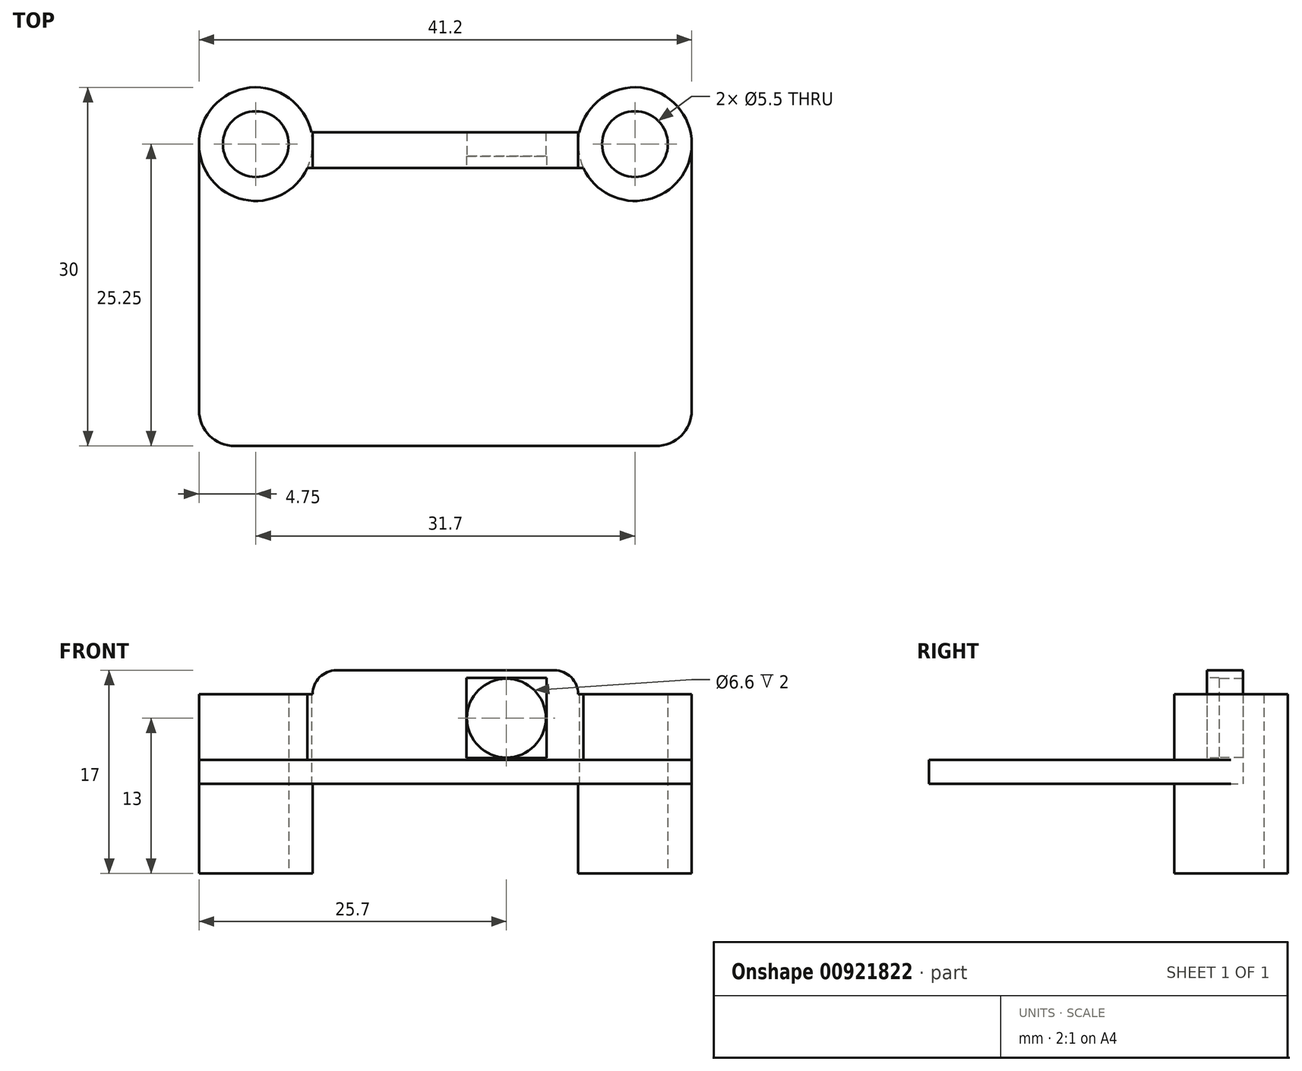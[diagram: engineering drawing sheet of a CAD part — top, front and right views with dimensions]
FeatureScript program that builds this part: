
annotation { "Feature Type Name" : "Feature", "Feature Type Description" : "" }
export const myFeature = defineFeature(function(context is Context, id is Id, definition is map)
    precondition{}
    {
        {
            var Q0;
            Q0=qCreatedBy(makeId("Top.planeOp"),FACE);
            var sketch = newSketch(context, id + "F0", { "sketchPlane" : qUnion([Q0])});
            skLineSegment(sketch, "E0.bottom", {"start": v(15.85, 15) * mm, "end": v(-15.85, 15) * mm});
            skLineSegment(sketch, "E0.top", {"start": v(17.6, -15) * mm, "end": v(-17.6, -15) * mm});
            skLineSegment(sketch, "E0.left", {"start": v(20.6, 10.25) * mm, "end": v(20.6, -12) * mm});
            skLineSegment(sketch, "E0.right", {"start": v(-20.6, 10.25) * mm, "end": v(-20.6, -12) * mm});
            skPoint(sketch, "E0.middle", {"position": v(0, 0) * mm});
            skCircle(sketch, "E1", {"center": v(-15.85, 10.25) * mm, "radius": 2.75 * mm});
            skLineSegment(sketch, "E2", {"start": v(-15.85, 10.25) * mm, "end": v(15.85, 10.25) * mm, "construction": true});
            skCircle(sketch, "E3", {"center": v(15.85, 10.25) * mm, "radius": 2.75 * mm});
            skPoint(sketch, "E4.visualSharp", {"position": v(-20.6, 15) * mm});
            skPoint(sketch, "E5.visualSharp", {"position": v(20.6, 15) * mm});
            skPoint(sketch, "E6.visualSharp", {"position": v(20.6, -15) * mm});
            skArc(sketch, "E6.filletArc", {"start": v(17.6, -15) * mm, "mid": v(19.72, -14.12) * mm, "end": v(20.6, -12) * mm});
            skPoint(sketch, "E7.visualSharp", {"position": v(-20.6, -15) * mm});
            skArc(sketch, "E7.filletArc", {"start": v(-20.6, -12) * mm, "mid": v(-19.72, -14.12) * mm, "end": v(-17.6, -15) * mm});
            skCircle(sketch, "E8.0", {"center": v(-15.85, 10.25) * mm, "radius": 4.75 * mm});
            skCircle(sketch, "E9.0", {"center": v(15.85, 10.25) * mm, "radius": 4.75 * mm});
            skSolve(sketch);
        }
        {
            var Q0;
            {var subQ2=sQuery(id+"F0.wireOp",EDGE,"E0.bottom");Q0=makeQuery(id+"F0.imprint","IMPRINT",FACE,{"disambiguationData":[TD([[makeQuery(id+"F0.imprint","IMPRINT",EDGE,{"derivedFrom":subQ2}),1.0]])]});}
            extrude(context, id + "F1", {"entities" : qUnion([Q0]), "depth" : 2 * mm, "offsetDistance" : 25 * mm});
        }
        {
            var Q0;
            Q0=makeQuery(id+"F0.imprint","IMPRINT",FACE,{"disambiguationData":[TD([[makeQuery(id+"F0.imprint","IMPRINT",EDGE,{"derivedFrom":sQuery(id+"F0.wireOp",EDGE,"E1")}),-1.0]])]});
            var Q1;
            Q1=makeQuery(id+"F0.imprint","IMPRINT",FACE,{"disambiguationData":[TD([[makeQuery(id+"F0.imprint","IMPRINT",EDGE,{"derivedFrom":sQuery(id+"F0.wireOp",EDGE,"E3")}),-1.0]])]});
            extrude(context, id + "F2", {"entities" : qUnion([Q0, Q1]), "operationType" : NewBodyOperationType.ADD, "endBound" : BoundingType.SYMMETRIC, "depth" : 15 * mm, "offsetDistance" : 25 * mm});
        }
        {
            var Q0;
            Q0=sQuery(id+"F0.wireOp",EDGE,"E2");
            cPlane(context, id + "F3", {"entities" : qUnion([Q0]), "cplaneType" : CPlaneType.LINE_ANGLE, "offset" : 25 * mm, "angle" : 0 * degree, "width" : 150 * mm, "height" : 150 * mm});
        }
        {
            var Q0;
            Q0=qCreatedBy(id+"F3.planeOp",FACE);
            var sketch = newSketch(context, id + "F4", { "sketchPlane" : qUnion([Q0])});
            skLineSegment(sketch, "E10", {"start": v(-11.1, 7.5) * mm, "end": v(-11.1, 7.5) * mm});
            skLineSegment(sketch, "E11", {"start": v(11.1, -7.5) * mm, "end": v(11.1, 2) * mm});
            skLineSegment(sketch, "E12.0", {"start": v(-15.85, 2) * mm, "end": v(15.85, 2) * mm});
            skLineSegment(sketch, "E13", {"start": v(-9.1, 9.5) * mm, "end": v(9.1, 9.5) * mm});
            skPoint(sketch, "E14.visualSharp", {"position": v(-11.1, 9.5) * mm});
            skArc(sketch, "E14.filletArc", {"start": v(-9.1, 9.5) * mm, "mid": v(-10.51, 8.91) * mm, "end": v(-11.1, 7.5) * mm});
            skPoint(sketch, "E15.visualSharp", {"position": v(11.1, 9.5) * mm});
            skArc(sketch, "E15.filletArc", {"start": v(11.1, 7.5) * mm, "mid": v(10.51, 8.91) * mm, "end": v(9.1, 9.5) * mm});
            skCircle(sketch, "E16", {"center": v(-5.1, 5.5) * mm, "radius": 3.3 * mm});
            skLineSegment(sketch, "E17.0", {"start": v(-20.6, 7.5) * mm, "end": v(-11.1, 7.5) * mm});
            skLineSegment(sketch, "E18", {"start": v(-13.1, 7.5) * mm, "end": v(-13.1, 2) * mm});
            skLineSegment(sketch, "E19.MirrorCS", {"start": v(13.1, 7.5) * mm, "end": v(13.1, 2) * mm});
            skLineSegment(sketch, "E20.trimOffspring", {"start": v(-11.1, 2) * mm, "end": v(-11.1, -7.5) * mm});
            skLineSegment(sketch, "E21.0", {"start": v(11.1, 7.5) * mm, "end": v(20.6, 7.5) * mm});
            skLineSegment(sketch, "E22.trimOffspring", {"start": v(11.1, 7.5) * mm, "end": v(11.1, 7.5) * mm});
            skSolve(sketch);
        }
        {
            var Q0;
            Q0 = qSketchRegion(id + "F4", true);
            extrude(context, id + "F5", {"entities" : qUnion([Q0]), "operationType" : NewBodyOperationType.ADD, "depth" : 1 * mm, "offsetDistance" : 25 * mm, "hasSecondDirection" : true, "secondDirectionOppositeDirection" : true, "secondDirectionDepth" : 2 * mm});
        }
        {
            var Q0;
            {var subQ0=sQuery(id+"F0.wireOp",EDGE,"E0.bottom");var subQ1=sQuery(id+"F0.wireOp",EDGE,"E8.0");var subQ2=sQuery(id+"F0.wireOp",EDGE,"E9.0");Q0=makeQuery(id+"F5.boolean.opBoolean","SPLIT",FACE,{"disambiguationData":[TD([makeQuery(id+"F1.opExtrude","SWEPT_FACE",FACE,{"disambiguationData":[OSD([subQ0])]})])],"derivedFrom":makeQuery(id+"F1.opExtrude","CAP_FACE",FACE,{"disambiguationData":[OSD([subQ0,sQuery(id+"F0.wireOp",EDGE,"E0.top"),sQuery(id+"F0.wireOp",EDGE,"E0.left"),sQuery(id+"F0.wireOp",EDGE,"E0.right"),sQuery(id+"F0.wireOp",EDGE,"E6.filletArc"),sQuery(id+"F0.wireOp",EDGE,"E7.filletArc"),subQ1,subQ2])],"isStart":false})});}
            var sketch = newSketch(context, id + "F6", { "sketchPlane" : qUnion([Q0])});
            skLineSegment(sketch, "E23.0.0", {"start": v(-11.2, 11.25) * mm, "end": v(11.2, 11.25) * mm});
            skArc(sketch, "E23.0.1", {"start": v(11.2, 11.25) * mm, "mid": v(12.87, 13.95) * mm, "end": v(15.85, 15) * mm});
            skLineSegment(sketch, "E23.0.2", {"start": v(15.85, 15) * mm, "end": v(-15.85, 15) * mm});
            skArc(sketch, "E23.0.3", {"start": v(-15.85, 15) * mm, "mid": v(-12.87, 13.95) * mm, "end": v(-11.2, 11.25) * mm});
            skSolve(sketch);
        }
        {
            var Q0;
            Q0 = qSketchRegion(id + "F6", true);
            var Q1;
            Q1=makeQuery(id+"F1.opExtrude","CAP_FACE",FACE,{"disambiguationData":[OSD([sQuery(id+"F0.wireOp",EDGE,"E0.bottom"),sQuery(id+"F0.wireOp",EDGE,"E0.top"),sQuery(id+"F0.wireOp",EDGE,"E0.left"),sQuery(id+"F0.wireOp",EDGE,"E0.right"),sQuery(id+"F0.wireOp",EDGE,"E6.filletArc"),sQuery(id+"F0.wireOp",EDGE,"E7.filletArc"),sQuery(id+"F0.wireOp",EDGE,"E8.0"),sQuery(id+"F0.wireOp",EDGE,"E9.0")])],"isStart":true});
            extrude(context, id + "F7", {"entities" : qUnion([Q0]), "operationType" : NewBodyOperationType.REMOVE, "endBound" : BoundingType.UP_TO_SURFACE, "oppositeDirection" : true, "depth" : 25 * mm, "endBoundEntityFace" : qUnion([Q1]), "offsetDistance" : 25 * mm});
        }
        {
            var Q0;
            Q0=makeQuery(id+"F5.opExtrude","CAP_FACE",FACE,{"disambiguationData":[OSD([sQuery(id+"F4.wireOp",EDGE,"E10"),sQuery(id+"F4.wireOp",EDGE,"E12.0"),sQuery(id+"F4.wireOp",EDGE,"E13"),sQuery(id+"F4.wireOp",EDGE,"E14.filletArc"),sQuery(id+"F4.wireOp",EDGE,"E15.filletArc"),sQuery(id+"F4.wireOp",EDGE,"E16"),sQuery(id+"F4.wireOp",EDGE,"E17.0"),sQuery(id+"F4.wireOp",EDGE,"E18"),sQuery(id+"F4.wireOp",EDGE,"E19.MirrorCS"),sQuery(id+"F4.wireOp",EDGE,"E21.0"),sQuery(id+"F4.wireOp",EDGE,"E22.trimOffspring")])],"isStart":true});
            var sketch = newSketch(context, id + "F8", { "sketchPlane" : qUnion([Q0])});
            skCircle(sketch, "E24.0", {"center": v(5.1, 5.5) * mm, "radius": 3.3 * mm});
            skLineSegment(sketch, "E25.bottom", {"start": v(1.75, 8.85) * mm, "end": v(8.45, 8.85) * mm});
            skLineSegment(sketch, "E25.top", {"start": v(1.75, 2.15) * mm, "end": v(8.45, 2.15) * mm});
            skLineSegment(sketch, "E25.left", {"start": v(1.75, 8.85) * mm, "end": v(1.75, 2.15) * mm});
            skLineSegment(sketch, "E25.right", {"start": v(8.45, 8.85) * mm, "end": v(8.45, 2.15) * mm});
            skSolve(sketch);
        }
        {
            var Q0;
            Q0=makeQuery(id+"F8.imprint","IMPRINT",FACE,{"disambiguationData":[TD([[makeQuery(id+"F8.imprint","IMPRINT",EDGE,{"derivedFrom":sQuery(id+"F8.wireOp",EDGE,"E24.0")}),1.0]])]});
            extrude(context, id + "F9", {"entities" : qUnion([Q0]), "operationType" : NewBodyOperationType.REMOVE, "oppositeDirection" : true, "depth" : 1 * mm, "offsetDistance" : 25 * mm});
        }
    });
